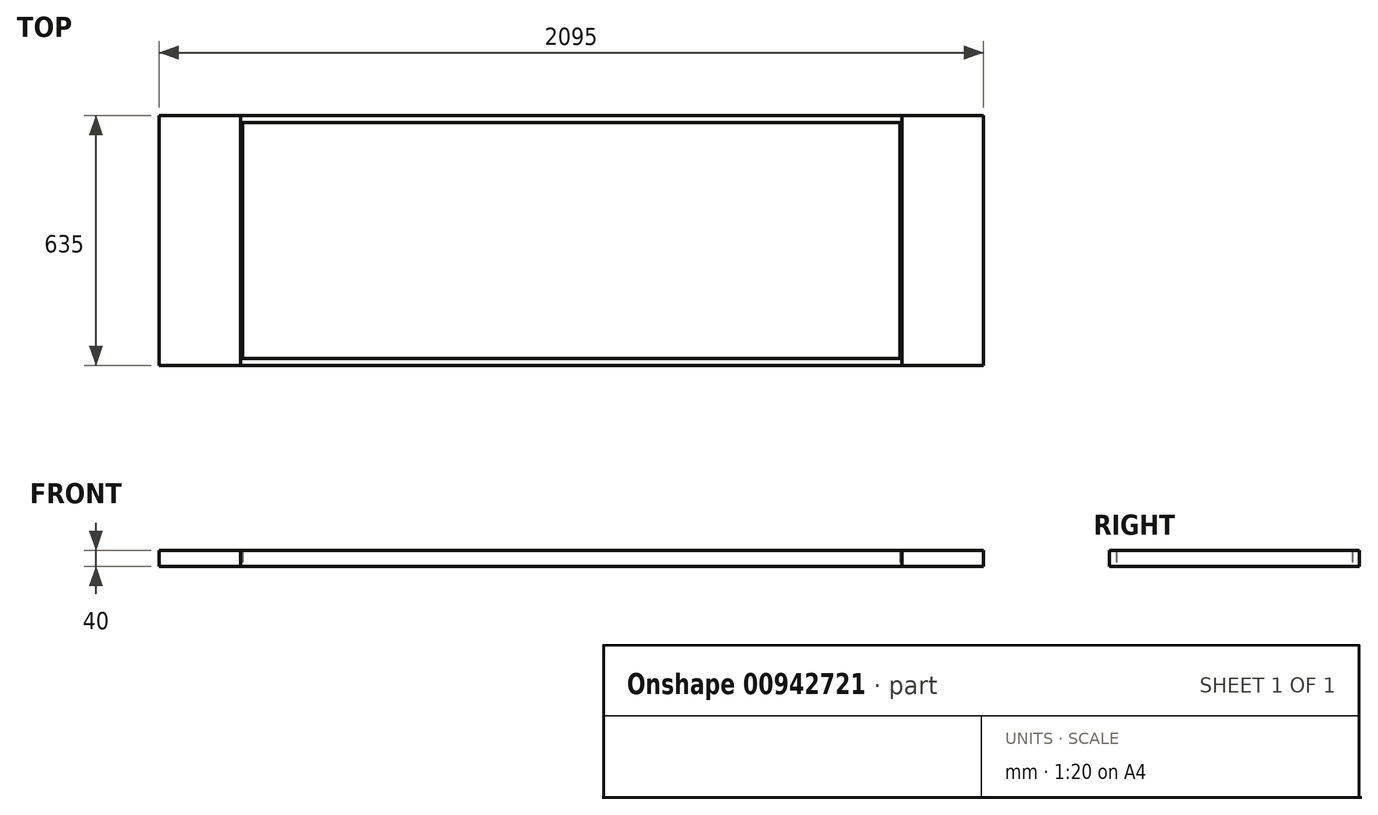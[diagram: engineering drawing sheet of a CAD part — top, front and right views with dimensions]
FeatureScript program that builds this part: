
annotation { "Feature Type Name" : "Feature", "Feature Type Description" : "" }
export const myFeature = defineFeature(function(context is Context, id is Id, definition is map)
    precondition{}
    {
        {
            var Q0;
            Q0=qCreatedBy(makeId("Top.planeOp"),FACE);
            var sketch = newSketch(context, id + "F0", { "sketchPlane" : qUnion([Q0])});
            skLineSegment(sketch, "E0.bottom", {"start": v(-1047.5, 317.5) * mm, "end": v(1047.5, 317.5) * mm});
            skLineSegment(sketch, "E0.top", {"start": v(-1047.5, -317.5) * mm, "end": v(1047.5, -317.5) * mm});
            skLineSegment(sketch, "E0.left", {"start": v(-1047.5, 317.5) * mm, "end": v(-1047.5, -317.5) * mm});
            skLineSegment(sketch, "E0.right", {"start": v(1047.5, 317.5) * mm, "end": v(1047.5, -317.5) * mm});
            skLineSegment(sketch, "E1", {"start": v(-1047.5, 0) * mm, "end": v(0, 0) * mm, "construction": true});
            skLineSegment(sketch, "E2", {"start": v(0, 0) * mm, "end": v(1047.5, 0) * mm, "construction": true});
            skLineSegment(sketch, "E3", {"start": v(0, -317.5) * mm, "end": v(0, 0) * mm, "construction": true});
            skLineSegment(sketch, "E4", {"start": v(0, 0) * mm, "end": v(0, 317.5) * mm, "construction": true});
            skSolve(sketch);
        }
        {
            var Q0;
            Q0 = qSketchRegion(id + "F0", true);
            extrude(context, id + "F1", {"entities" : qUnion([Q0]), "depth" : 40 * mm, "offsetDistance" : 25 * mm});
        }
        {
            var Q0;
            Q0=qCreatedBy(makeId("Top.planeOp"),FACE);
            var sketch = newSketch(context, id + "F2", { "sketchPlane" : qUnion([Q0])});
            skLineSegment(sketch, "E5.bottom", {"start": v(-835, 300) * mm, "end": v(835, 300) * mm});
            skLineSegment(sketch, "E5.top", {"start": v(-835, -300) * mm, "end": v(835, -300) * mm});
            skLineSegment(sketch, "E5.left", {"start": v(-835, 300) * mm, "end": v(-835, -300) * mm});
            skLineSegment(sketch, "E5.right", {"start": v(835, 300) * mm, "end": v(835, -300) * mm});
            skLineSegment(sketch, "E6", {"start": v(-835, 0) * mm, "end": v(0, 0) * mm, "construction": true});
            skLineSegment(sketch, "E7", {"start": v(0, 0) * mm, "end": v(835, 0) * mm, "construction": true});
            skLineSegment(sketch, "E8", {"start": v(0, -300) * mm, "end": v(0, 0) * mm, "construction": true});
            skLineSegment(sketch, "E9", {"start": v(0, 0) * mm, "end": v(0, 300) * mm, "construction": true});
            skSolve(sketch);
        }
        {
            var Q0;
            Q0 = qSketchRegion(id + "F2", true);
            extrude(context, id + "F3", {"entities" : qUnion([Q0]), "depth" : 40 * mm, "offsetDistance" : 25 * mm});
        }
        {
            var Q0;
            Q0=qCreatedBy(makeId("Top.planeOp"),FACE);
            var sketch = newSketch(context, id + "F4", { "sketchPlane" : qUnion([Q0])});
            skLineSegment(sketch, "E10.bottom", {"start": v(-840, 317.5) * mm, "end": v(840, 317.5) * mm});
            skLineSegment(sketch, "E10.top", {"start": v(-840, -317.5) * mm, "end": v(840, -317.5) * mm});
            skLineSegment(sketch, "E10.left", {"start": v(-840, 317.5) * mm, "end": v(-840, -317.5) * mm});
            skLineSegment(sketch, "E10.right", {"start": v(840, 317.5) * mm, "end": v(840, -317.5) * mm});
            skLineSegment(sketch, "E11", {"start": v(-840, 0) * mm, "end": v(0, 0) * mm, "construction": true});
            skLineSegment(sketch, "E12", {"start": v(0, 0) * mm, "end": v(840, 0) * mm, "construction": true});
            skLineSegment(sketch, "E13", {"start": v(0, -317.5) * mm, "end": v(0, 0) * mm, "construction": true});
            skLineSegment(sketch, "E14", {"start": v(0, 0) * mm, "end": v(0, 317.5) * mm, "construction": true});
            skSolve(sketch);
        }
        {
            var Q0;
            Q0 = qSketchRegion(id + "F4", true);
            extrude(context, id + "F5", {"entities" : qUnion([Q0]), "depth" : 40 * mm, "offsetDistance" : 25 * mm});
        }
    });
